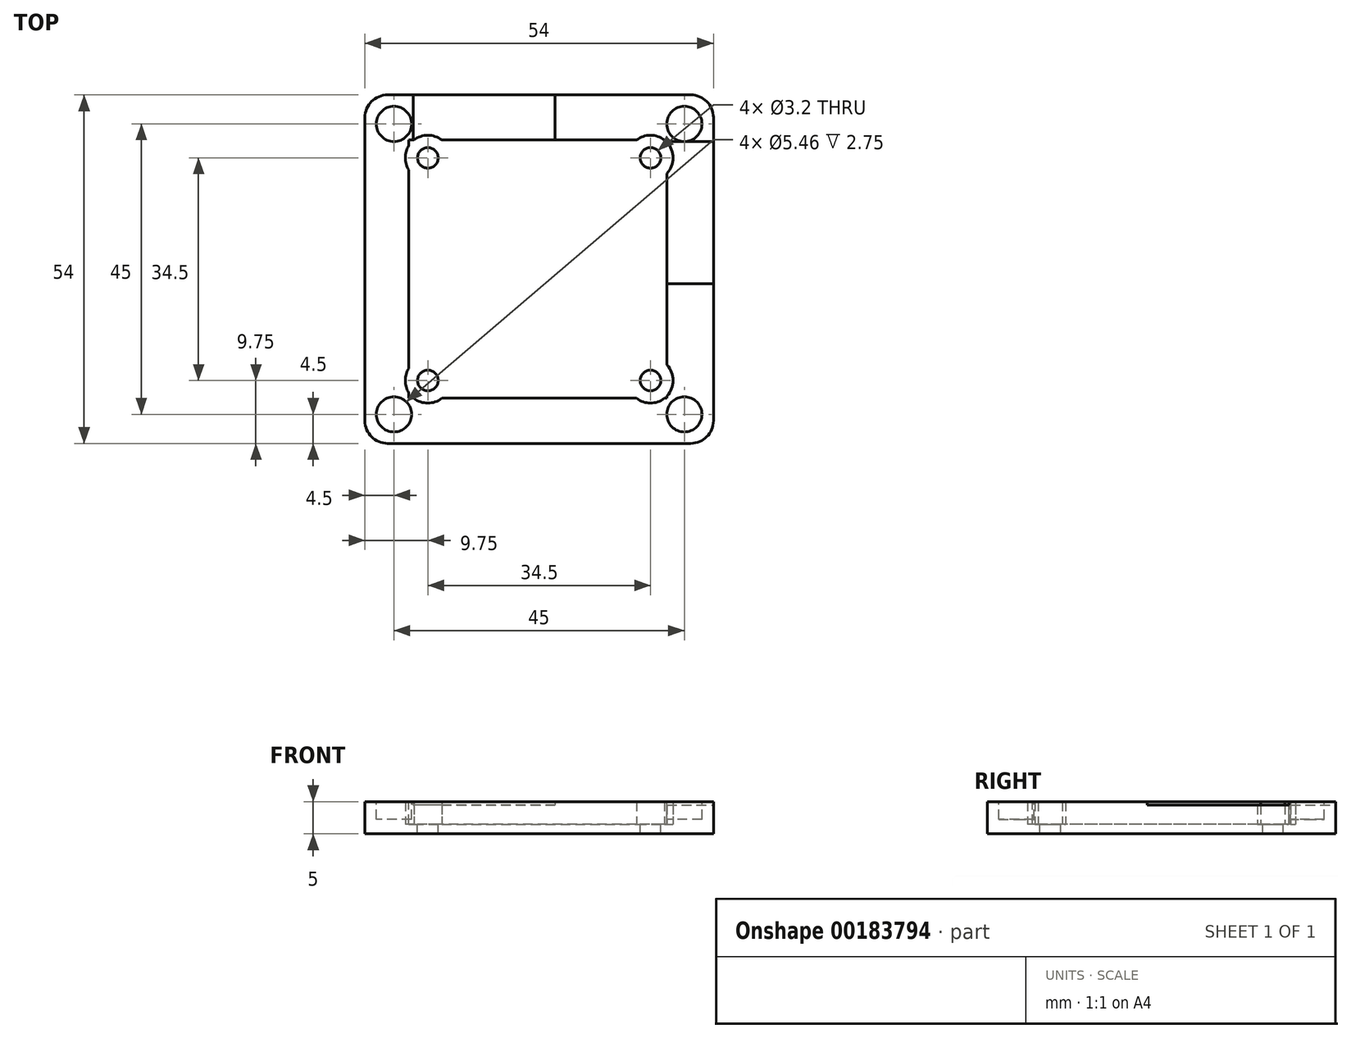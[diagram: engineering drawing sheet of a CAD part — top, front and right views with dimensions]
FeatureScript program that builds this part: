
annotation { "Feature Type Name" : "Feature", "Feature Type Description" : "" }
export const myFeature = defineFeature(function(context is Context, id is Id, definition is map)
    precondition{}
    {
        {
            var Q0;
            Q0=qCreatedBy(makeId("Top.planeOp"),FACE);
            var sketch = newSketch(context, id + "F0", { "sketchPlane" : qUnion([Q0])});
            skLineSegment(sketch, "E0", {"start": v(27, 0) * mm, "end": v(27, 27) * mm});
            skLineSegment(sketch, "E1", {"start": v(27, 27) * mm, "end": v(-27, 27) * mm});
            skLineSegment(sketch, "E2", {"start": v(-27, 27) * mm, "end": v(-27, -27) * mm});
            skLineSegment(sketch, "E3", {"start": v(-27, -27) * mm, "end": v(27, -27) * mm});
            skLineSegment(sketch, "E4", {"start": v(27, -27) * mm, "end": v(27, 0) * mm});
            skSolve(sketch);
        }
        {
            var Q0;
            Q0 = qSketchRegion(id + "F0", true);
            extrude(context, id + "F1", {"entities" : qUnion([Q0]), "depth" : 5 * mm});
        }
        {
            var Q0;
            Q0=makeQuery(id+"F1.opExtrude","CAP_FACE",FACE,{"disambiguationData":[OSD([sQuery(id+"F0.wireOp",EDGE,"E0"),sQuery(id+"F0.wireOp",EDGE,"E1"),sQuery(id+"F0.wireOp",EDGE,"E2"),sQuery(id+"F0.wireOp",EDGE,"E3"),sQuery(id+"F0.wireOp",EDGE,"E4")])],"isStart":false});
            var sketch = newSketch(context, id + "F2", { "sketchPlane" : qUnion([Q0])});
            skCircle(sketch, "E5", {"center": v(-22.5, 22.5) * mm, "radius": 2.73 * mm});
            skCircle(sketch, "E6", {"center": v(22.5, 22.5) * mm, "radius": 2.73 * mm});
            skCircle(sketch, "E7", {"center": v(22.5, -22.5) * mm, "radius": 2.73 * mm});
            skCircle(sketch, "E8", {"center": v(-22.5, -22.5) * mm, "radius": 2.73 * mm});
            skSolve(sketch);
        }
        {
            var Q0;
            Q0=makeQuery(id+"F1.opExtrude","CAP_FACE",FACE,{"disambiguationData":[OSD([sQuery(id+"F0.wireOp",EDGE,"E0"),sQuery(id+"F0.wireOp",EDGE,"E1"),sQuery(id+"F0.wireOp",EDGE,"E2"),sQuery(id+"F0.wireOp",EDGE,"E3"),sQuery(id+"F0.wireOp",EDGE,"E4")])],"isStart":true});
            extrude(context, id + "F3", {"entities" : qUnion([Q0]), "operationType" : NewBodyOperationType.ADD, "depth" : 1.2 * mm});
        }
        {
            var Q0;
            Q0 = qSketchRegion(id + "F2", true);
            extrude(context, id + "F4", {"entities" : qUnion([Q0]), "operationType" : NewBodyOperationType.REMOVE, "oppositeDirection" : true, "depth" : 3.75 * mm});
        }
        {
            var Q0;
            Q0=makeQuery(id+"F1.opExtrude","CAP_FACE",FACE,{"disambiguationData":[OSD([sQuery(id+"F0.wireOp",EDGE,"E0"),sQuery(id+"F0.wireOp",EDGE,"E1"),sQuery(id+"F0.wireOp",EDGE,"E2"),sQuery(id+"F0.wireOp",EDGE,"E3"),sQuery(id+"F0.wireOp",EDGE,"E4")])],"isStart":false});
            var sketch = newSketch(context, id + "F5", { "sketchPlane" : qUnion([Q0])});
            skLineSegment(sketch, "E9", {"start": v(19.8, 20) * mm, "end": v(-20.2, 20) * mm});
            skLineSegment(sketch, "E10", {"start": v(-20.2, 20) * mm, "end": v(-20.2, -20) * mm});
            skLineSegment(sketch, "E11", {"start": v(-20.2, -20) * mm, "end": v(19.8, -20) * mm});
            skLineSegment(sketch, "E12", {"start": v(19.8, 20) * mm, "end": v(19.8, -20) * mm});
            skSolve(sketch);
        }
        {
            var Q0;
            Q0 = qSketchRegion(id + "F5", true);
            extrude(context, id + "F6", {"entities" : qUnion([Q0]), "operationType" : NewBodyOperationType.REMOVE, "oppositeDirection" : true, "depth" : 3 * mm});
        }
        {
            var Q0;
            Q0=makeQuery(id+"F6.boolean.opBoolean","COPY",FACE,{"derivedFrom":makeQuery(id+"F6.opExtrude","CAP_FACE",FACE,{"disambiguationData":[OSD([sQuery(id+"F5.wireOp",EDGE,"E9"),sQuery(id+"F5.wireOp",EDGE,"E10"),sQuery(id+"F5.wireOp",EDGE,"E11"),sQuery(id+"F5.wireOp",EDGE,"E12")])],"isStart":false})});
            var sketch = newSketch(context, id + "F7", { "sketchPlane" : qUnion([Q0])});
            skCircle(sketch, "E13", {"center": v(17.25, 17.25) * mm, "radius": 1.6 * mm});
            skCircle(sketch, "E14", {"center": v(-17.25, 17.25) * mm, "radius": 1.6 * mm});
            skCircle(sketch, "E15", {"center": v(-17.25, -17.25) * mm, "radius": 1.6 * mm});
            skCircle(sketch, "E16", {"center": v(17.25, -17.25) * mm, "radius": 1.6 * mm});
            skSolve(sketch);
        }
        {
            var Q0;
            Q0 = qSketchRegion(id + "F7", true);
            extrude(context, id + "F8", {"entities" : qUnion([Q0]), "operationType" : NewBodyOperationType.REMOVE, "oppositeDirection" : true, "depth" : 3.2 * mm});
        }
        {
            var Q0;
            Q0=makeQuery(id+"F1.opExtrude","CAP_FACE",FACE,{"disambiguationData":[OSD([sQuery(id+"F0.wireOp",EDGE,"E0"),sQuery(id+"F0.wireOp",EDGE,"E1"),sQuery(id+"F0.wireOp",EDGE,"E2"),sQuery(id+"F0.wireOp",EDGE,"E3"),sQuery(id+"F0.wireOp",EDGE,"E4")])],"isStart":false});
            extrude(context, id + "F9", {"entities" : qUnion([Q0]), "operationType" : NewBodyOperationType.REMOVE, "oppositeDirection" : true, "depth" : 1 * mm});
        }
        {
            var Q0;
            Q0=makeQuery(id+"F3.opExtrude","CAP_FACE",FACE,{"disambiguationData":[OSD([sQuery(id+"F0.wireOp",EDGE,"E0"),sQuery(id+"F0.wireOp",EDGE,"E1"),sQuery(id+"F0.wireOp",EDGE,"E2"),sQuery(id+"F0.wireOp",EDGE,"E3"),sQuery(id+"F0.wireOp",EDGE,"E4")])],"isStart":false});
            extrude(context, id + "F10", {"entities" : qUnion([Q0]), "operationType" : NewBodyOperationType.REMOVE, "oppositeDirection" : true, "depth" : 0.2 * mm});
        }
        {
            var Q0;
            {var subQ0=sQuery(id+"F0.wireOp",EDGE,"E2");var subQ1=sQuery(id+"F0.wireOp",EDGE,"E1");Q0=makeQuery(id+"F3.boolean.opBoolean","MERGE",EDGE,{"derivedFrom":[makeQuery(id+"F1.opExtrude","SWEPT_EDGE",EDGE,{"disambiguationData":[OSD([subQ1,subQ0])]}),makeQuery(id+"F3.opExtrude","SWEPT_EDGE",EDGE,{"disambiguationData":[OSD([subQ1,subQ0])]})]});}
            var Q1;
            {var subQ0=sQuery(id+"F0.wireOp",EDGE,"E3");var subQ1=sQuery(id+"F0.wireOp",EDGE,"E2");Q1=makeQuery(id+"F3.boolean.opBoolean","MERGE",EDGE,{"derivedFrom":[makeQuery(id+"F1.opExtrude","SWEPT_EDGE",EDGE,{"disambiguationData":[OSD([subQ1,subQ0])]}),makeQuery(id+"F3.opExtrude","SWEPT_EDGE",EDGE,{"disambiguationData":[OSD([subQ1,subQ0])]})]});}
            var Q2;
            {var subQ0=sQuery(id+"F0.wireOp",EDGE,"E4");var subQ1=sQuery(id+"F0.wireOp",EDGE,"E3");Q2=makeQuery(id+"F3.boolean.opBoolean","MERGE",EDGE,{"derivedFrom":[makeQuery(id+"F1.opExtrude","SWEPT_EDGE",EDGE,{"disambiguationData":[OSD([subQ1,subQ0])]}),makeQuery(id+"F3.opExtrude","SWEPT_EDGE",EDGE,{"disambiguationData":[OSD([subQ1,subQ0])]})]});}
            var Q3;
            {var subQ0=sQuery(id+"F0.wireOp",EDGE,"E1");var subQ1=sQuery(id+"F0.wireOp",EDGE,"E0");Q3=makeQuery(id+"F3.boolean.opBoolean","MERGE",EDGE,{"derivedFrom":[makeQuery(id+"F1.opExtrude","SWEPT_EDGE",EDGE,{"disambiguationData":[OSD([subQ1,subQ0])]}),makeQuery(id+"F3.opExtrude","SWEPT_EDGE",EDGE,{"disambiguationData":[OSD([subQ1,subQ0])]})]});}
            fillet(context, id + "F11", {"entities" : qUnion([Q0, Q1, Q2, Q3]), "radius" : 3.5 * mm, "tangentPropagation" : true, "allowEdgeOverflow" : false});
        }
        {
            var Q0;
            Q0=makeQuery(id+"F6.boolean.opBoolean","COPY",FACE,{"derivedFrom":makeQuery(id+"F6.opExtrude","CAP_FACE",FACE,{"disambiguationData":[OSD([sQuery(id+"F5.wireOp",EDGE,"E9"),sQuery(id+"F5.wireOp",EDGE,"E10"),sQuery(id+"F5.wireOp",EDGE,"E11"),sQuery(id+"F5.wireOp",EDGE,"E12")])],"isStart":false})});
            var sketch = newSketch(context, id + "F12", { "sketchPlane" : qUnion([Q0])});
            skCircle(sketch, "E17", {"center": v(17.25, 17.25) * mm, "radius": 3.5 * mm});
            skCircle(sketch, "E18", {"center": v(17.25, -17.25) * mm, "radius": 3.5 * mm});
            skCircle(sketch, "E19", {"center": v(-17.25, -17.25) * mm, "radius": 3.5 * mm});
            skCircle(sketch, "E20", {"center": v(-17.25, 17.25) * mm, "radius": 3.5 * mm});
            skSolve(sketch);
        }
        {
            var Q0;
            Q0 = qSketchRegion(id + "F12", true);
            extrude(context, id + "F13", {"entities" : qUnion([Q0]), "operationType" : NewBodyOperationType.REMOVE, "depth" : 2 * mm});
        }
        {
            var Q0;
            Q0=makeQuery(id+"F13.boolean.opBoolean","MERGE",FACE,{"derivedFrom":[makeQuery(id+"F6.boolean.opBoolean","COPY",FACE,{"derivedFrom":makeQuery(id+"F6.opExtrude","CAP_FACE",FACE,{"disambiguationData":[OSD([sQuery(id+"F5.wireOp",EDGE,"E9"),sQuery(id+"F5.wireOp",EDGE,"E10"),sQuery(id+"F5.wireOp",EDGE,"E11"),sQuery(id+"F5.wireOp",EDGE,"E12")])],"isStart":false})}),makeQuery(id+"F13.opExtrude","CAP_FACE",FACE,{"disambiguationData":[OSD([sQuery(id+"F12.wireOp",EDGE,"E17")])],"isStart":true}),makeQuery(id+"F13.opExtrude","CAP_FACE",FACE,{"disambiguationData":[OSD([sQuery(id+"F12.wireOp",EDGE,"E18")])],"isStart":true}),makeQuery(id+"F13.opExtrude","CAP_FACE",FACE,{"disambiguationData":[OSD([sQuery(id+"F12.wireOp",EDGE,"E19")])],"isStart":true}),makeQuery(id+"F13.opExtrude","CAP_FACE",FACE,{"disambiguationData":[OSD([sQuery(id+"F12.wireOp",EDGE,"E20")])],"isStart":true})]});
            extrude(context, id + "F14", {"entities" : qUnion([Q0]), "operationType" : NewBodyOperationType.REMOVE, "oppositeDirection" : true, "depth" : 0.5 * mm});
        }
        {
            var Q0;
            Q0=makeQuery(id+"F9.boolean.opBoolean","COPY",FACE,{"derivedFrom":makeQuery(id+"F9.opExtrude","CAP_FACE",FACE,{"disambiguationData":[OSD([sQuery(id+"F0.wireOp",EDGE,"E0"),sQuery(id+"F0.wireOp",EDGE,"E1"),sQuery(id+"F0.wireOp",EDGE,"E2"),sQuery(id+"F0.wireOp",EDGE,"E3"),sQuery(id+"F0.wireOp",EDGE,"E4")])],"isStart":false})});
            var sketch = newSketch(context, id + "F15", { "sketchPlane" : qUnion([Q0])});
            skLineSegment(sketch, "E21", {"start": v(19.8, -2.23) * mm, "end": v(27, -2.23) * mm});
            skLineSegment(sketch, "E22", {"start": v(27, -2.23) * mm, "end": v(27, 19.77) * mm});
            skLineSegment(sketch, "E23", {"start": v(27, 19.77) * mm, "end": v(19.8, 19.77) * mm});
            skLineSegment(sketch, "E24", {"start": v(19.8, 19.77) * mm, "end": v(19.8, -2.23) * mm});
            skLineSegment(sketch, "E25", {"start": v(2.47, 19.8) * mm, "end": v(2.47, 27) * mm});
            skLineSegment(sketch, "E26", {"start": v(2.47, 27) * mm, "end": v(-19.52, 27) * mm});
            skLineSegment(sketch, "E27", {"start": v(-19.52, 27) * mm, "end": v(-19.52, 19.8) * mm});
            skLineSegment(sketch, "E28", {"start": v(-19.52, 19.8) * mm, "end": v(2.47, 19.8) * mm});
            skSolve(sketch);
        }
        {
            var Q0;
            Q0 = qSketchRegion(id + "F15", true);
            extrude(context, id + "F16", {"entities" : qUnion([Q0]), "operationType" : NewBodyOperationType.REMOVE, "oppositeDirection" : true, "depth" : 0.5 * mm});
        }
        {
            var Q0;
            Q0=makeQuery(id+"F14.boolean.opBoolean","COPY",FACE,{"derivedFrom":makeQuery(id+"F14.opExtrude","CAP_FACE",FACE,{"disambiguationData":[OSD([sQuery(id+"F5.wireOp",EDGE,"E9"),sQuery(id+"F5.wireOp",EDGE,"E10"),sQuery(id+"F5.wireOp",EDGE,"E11"),sQuery(id+"F5.wireOp",EDGE,"E12"),sQuery(id+"F12.wireOp",EDGE,"E17"),sQuery(id+"F12.wireOp",EDGE,"E18"),sQuery(id+"F12.wireOp",EDGE,"E19"),sQuery(id+"F12.wireOp",EDGE,"E20")])],"isStart":false})});
            extrude(context, id + "F17", {"entities" : qUnion([Q0]), "operationType" : NewBodyOperationType.REMOVE, "oppositeDirection" : true, "depth" : 1 * mm});
        }
    });
